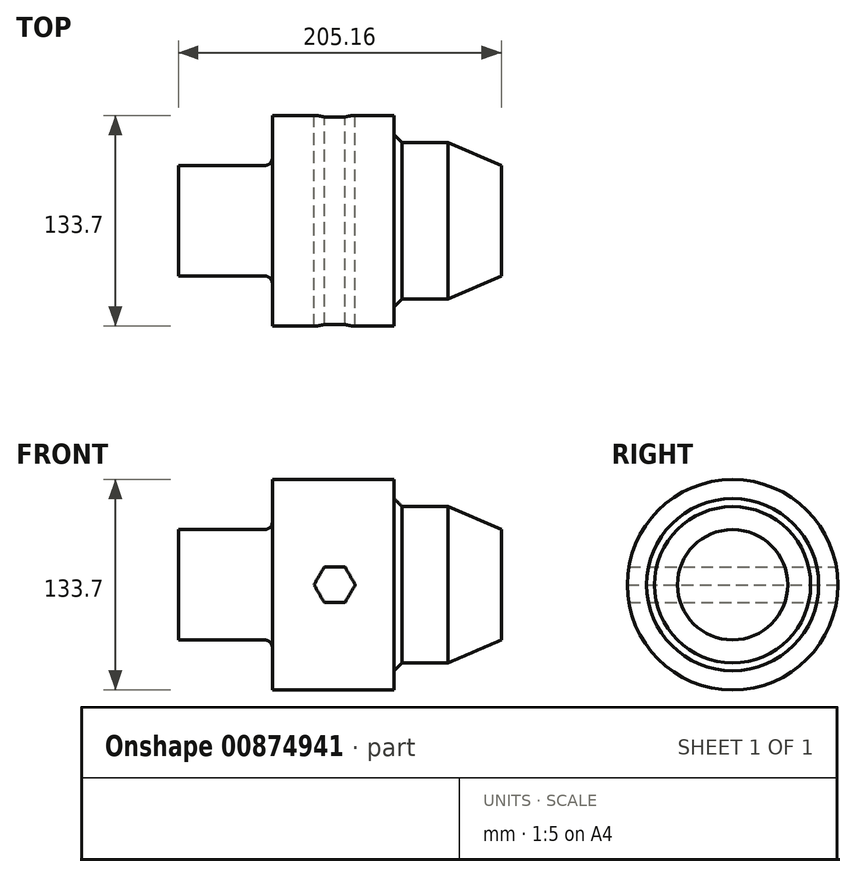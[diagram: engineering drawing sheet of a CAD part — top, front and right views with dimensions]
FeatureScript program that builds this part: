
annotation { "Feature Type Name" : "Feature", "Feature Type Description" : "" }
export const myFeature = defineFeature(function(context is Context, id is Id, definition is map)
    precondition{}
    {
        {
            var Q0;
            Q0=qCreatedBy(makeId("Front.planeOp"),FACE);
            var sketch = newSketch(context, id + "F0", { "sketchPlane" : qUnion([Q0])});
            skLineSegment(sketch, "E0", {"start": v(0, 0) * mm, "end": v(0, 35.04) * mm});
            skLineSegment(sketch, "E1", {"start": v(0, 35.04) * mm, "end": v(59.75, 35.04) * mm});
            skLineSegment(sketch, "E2", {"start": v(59.75, 35.04) * mm, "end": v(59.75, 66.85) * mm});
            skLineSegment(sketch, "E3", {"start": v(59.75, 66.85) * mm, "end": v(137.04, 66.85) * mm});
            skLineSegment(sketch, "E4", {"start": v(137.04, 66.85) * mm, "end": v(137.04, 49.58) * mm});
            skLineSegment(sketch, "E5", {"start": v(137.04, 49.58) * mm, "end": v(171.3, 49.58) * mm});
            skLineSegment(sketch, "E6", {"start": v(171.3, 49.58) * mm, "end": v(205.16, 35.04) * mm});
            skLineSegment(sketch, "E7", {"start": v(205.16, 35.04) * mm, "end": v(205.16, 0) * mm});
            skLineSegment(sketch, "E8", {"start": v(205.16, 0) * mm, "end": v(0, 0) * mm});
            skSolve(sketch);
        }
        {
            var Q0;
            Q0 = qSketchRegion(id + "F0", true);
            var Q1;
            Q1=sQuery(id+"F0.wireOp",EDGE,"E8");
            revolve(context, id + "F1", {"surfaceOperationType" : NewSurfaceOperationType.NEW, "entities" : qUnion([Q0]), "axis" : qUnion([Q1]), "revolveType" : RevolveType.FULL});
        }
        {
            var Q0;
            Q0=makeQuery(id+"F1.opRevolve","SWEPT_EDGE",EDGE,{"disambiguationData":[OSD([sQuery(id+"F0.wireOp",EDGE,"E1"),sQuery(id+"F0.wireOp",EDGE,"E2")])]});
            fillet(context, id + "F2", {"entities" : qUnion([Q0]), "radius" : 5.08 * mm, "tangentPropagation" : true, "allowEdgeOverflow" : false});
        }
        {
            var Q0;
            Q0=makeQuery(id+"F1.opRevolve","SWEPT_EDGE",EDGE,{"disambiguationData":[OSD([sQuery(id+"F0.wireOp",EDGE,"E4"),sQuery(id+"F0.wireOp",EDGE,"E5")])]});
            chamfer(context, id + "F3", {"entities" : qUnion([Q0]), "width" : 5.08 * mm, "tangentPropagation" : true});
        }
        {
            var Q0;
            Q0=qCreatedBy(makeId("Front.planeOp"),FACE);
            var sketch = newSketch(context, id + "F4", { "sketchPlane" : qUnion([Q0])});
            skCircle(sketch, "E9.cCircle", {"center": v(99.24, 0) * mm, "radius": 11.34 * mm, "construction": true});
            skLineSegment(sketch, "E9.0", {"start": v(105.79, -11.34) * mm, "end": v(92.69, -11.34) * mm});
            skLineSegment(sketch, "E9.1", {"start": v(92.69, -11.34) * mm, "end": v(86.14, 0) * mm});
            skLineSegment(sketch, "E9.2", {"start": v(86.14, 0) * mm, "end": v(92.69, 11.34) * mm});
            skLineSegment(sketch, "E9.3", {"start": v(92.69, 11.34) * mm, "end": v(105.79, 11.34) * mm});
            skLineSegment(sketch, "E9.4", {"start": v(105.79, 11.34) * mm, "end": v(112.34, 0) * mm});
            skLineSegment(sketch, "E9.5", {"start": v(112.34, 0) * mm, "end": v(105.79, -11.34) * mm});
            skPoint(sketch, "E9.0.midPoint", {"position": v(99.24, -11.34) * mm});
            skSolve(sketch);
        }
        {
            var Q0;
            Q0 = qSketchRegion(id + "F4", true);
            var Q1;
            Q1=makeQuery(id+"F1.opRevolve","SWEPT_FACE",FACE,{"disambiguationData":[OSD([sQuery(id+"F0.wireOp",EDGE,"E3")])]});
            var Q2;
            Q2=makeQuery(id+"F1.opRevolve","SWEPT_FACE",FACE,{"disambiguationData":[OSD([sQuery(id+"F0.wireOp",EDGE,"E3")])]});
            extrude(context, id + "F5", {"entities" : qUnion([Q0]), "operationType" : NewBodyOperationType.REMOVE, "endBound" : BoundingType.UP_TO_SURFACE, "depth" : 25.4 * mm, "endBoundEntityFace" : qUnion([Q1]), "offsetDistance" : 25.4 * mm, "hasSecondDirection" : true, "secondDirectionBound" : SecondDirectionBoundingType.UP_TO_SURFACE, "secondDirectionOppositeDirection" : true, "secondDirectionDepth" : 25.4 * mm, "secondDirectionBoundEntityFace" : qUnion([Q2])});
        }
    });
